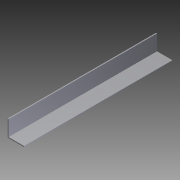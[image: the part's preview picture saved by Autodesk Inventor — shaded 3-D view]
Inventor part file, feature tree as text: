
AUTODESK INVENTOR PART (.ipt)
format: ipt  version: 2012 (Build 160160000, 160)  size: 73,728 bytes
history: native  units: in
note: dims shown in document units (in); Inventor stores cm internally (conversion verified against a paired STEP export)
features: extrude x1, sketch x1
ambient origin geometry x8: Origin, YZ Plane, XZ Plane, XY Plane, X Axis, Y Axis, Z Axis, Center Point
bodies: Solid1 (feature_tree)
feature tree (2):
  extrude  "Extrusion1"  Depth=1.0in
  sketch  "Sketch1"  dims[d0=1.0in d1=1.0in d2=0.0625in d3=0.0625in d4=9.0in d5=0.0in]
